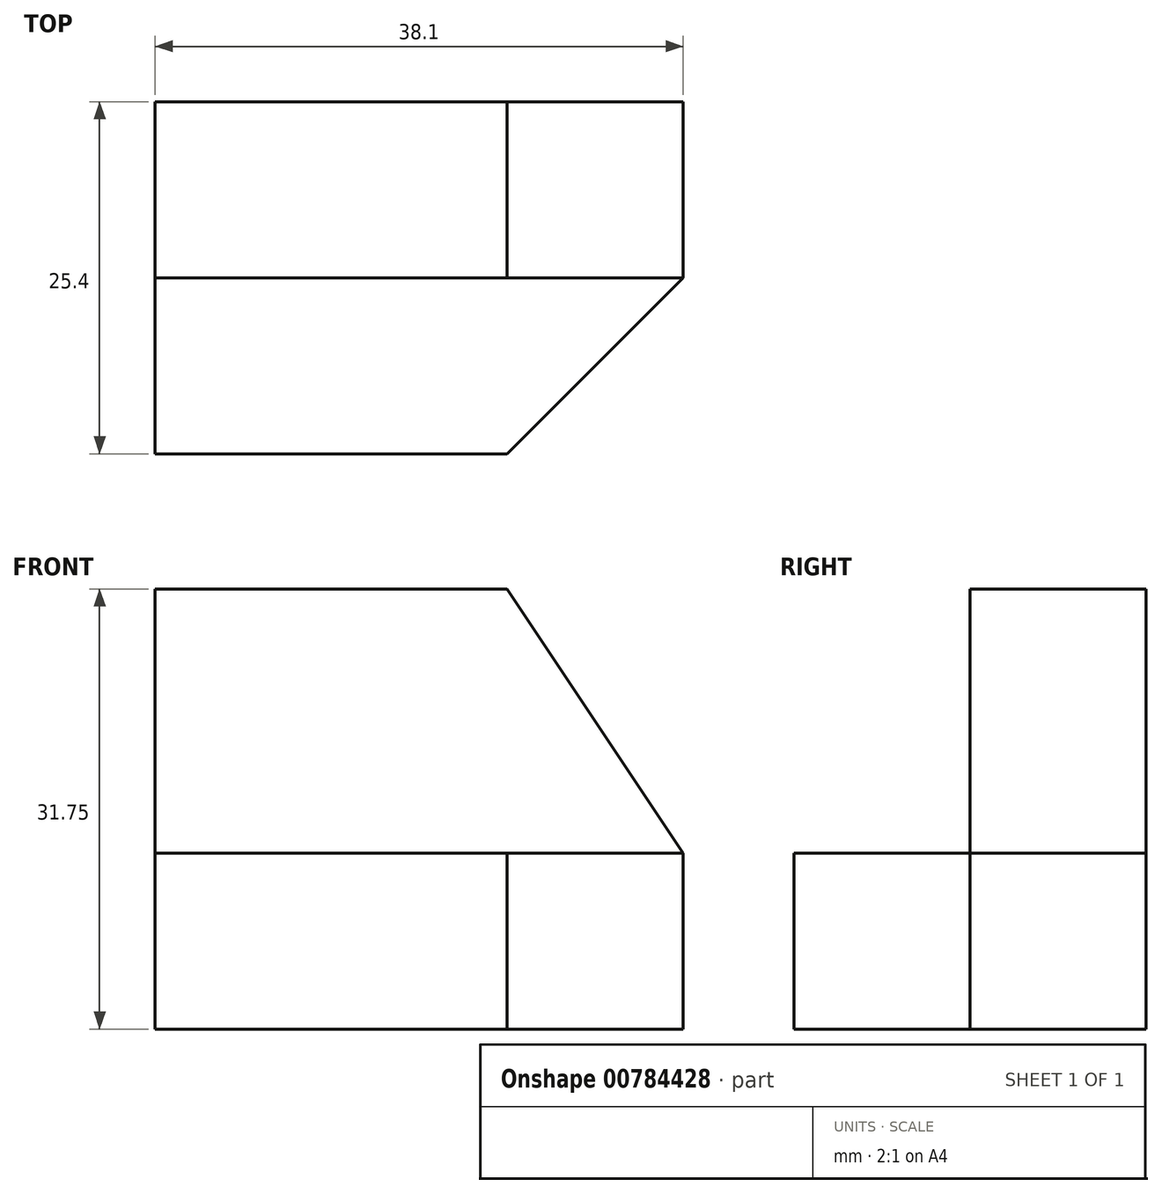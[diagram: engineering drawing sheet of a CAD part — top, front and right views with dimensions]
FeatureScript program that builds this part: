
annotation { "Feature Type Name" : "Feature", "Feature Type Description" : "" }
export const myFeature = defineFeature(function(context is Context, id is Id, definition is map)
    precondition{}
    {
        {
            var Q0;
            Q0=qCreatedBy(makeId("Front.planeOp"),FACE);
            var sketch = newSketch(context, id + "F0", { "sketchPlane" : qUnion([Q0])});
            skLineSegment(sketch, "E0", {"start": v(0, 0) * mm, "end": v(0, 31.75) * mm});
            skLineSegment(sketch, "E1", {"start": v(0, 31.75) * mm, "end": v(25.4, 31.75) * mm});
            skLineSegment(sketch, "E2", {"start": v(0, 0) * mm, "end": v(38.1, 0) * mm});
            skLineSegment(sketch, "E3", {"start": v(38.1, 0) * mm, "end": v(38.1, 12.7) * mm});
            skLineSegment(sketch, "E4", {"start": v(38.1, 12.7) * mm, "end": v(25.4, 31.75) * mm});
            skSolve(sketch);
        }
        {
            var Q0;
            Q0 = qSketchRegion(id + "F0", true);
            extrude(context, id + "F1", {"entities" : qUnion([Q0]), "depth" : 25.4 * mm, "offsetDistance" : 25.4 * mm});
        }
        {
            var Q0;
            Q0=makeQuery(id+"F1.opExtrude","SWEPT_FACE",FACE,{"disambiguationData":[OSD([sQuery(id+"F0.wireOp",EDGE,"E0")])]});
            var sketch = newSketch(context, id + "F2", { "sketchPlane" : qUnion([Q0])});
            skLineSegment(sketch, "E5", {"start": v(25.4, 31.75) * mm, "end": v(12.7, 31.75) * mm});
            skLineSegment(sketch, "E6", {"start": v(12.7, 31.75) * mm, "end": v(12.7, 12.7) * mm});
            skLineSegment(sketch, "E7", {"start": v(12.7, 12.7) * mm, "end": v(25.4, 12.7) * mm});
            skLineSegment(sketch, "E8", {"start": v(25.4, 12.7) * mm, "end": v(25.4, 31.75) * mm});
            skSolve(sketch);
        }
        {
            var Q0;
            Q0 = qSketchRegion(id + "F2", true);
            extrude(context, id + "F3", {"entities" : qUnion([Q0]), "operationType" : NewBodyOperationType.REMOVE, "oppositeDirection" : true, "depth" : 38.1 * mm, "offsetDistance" : 25.4 * mm});
        }
        {
            var Q0;
            Q0=makeQuery(id+"F3.boolean.opBoolean","COPY",FACE,{"derivedFrom":makeQuery(id+"F3.opExtrude","SWEPT_FACE",FACE,{"disambiguationData":[OSD([sQuery(id+"F2.wireOp",EDGE,"E7")])]})});
            var sketch = newSketch(context, id + "F4", { "sketchPlane" : qUnion([Q0])});
            skLineSegment(sketch, "E9", {"start": v(38.1, -25.4) * mm, "end": v(25.4, -25.4) * mm});
            skLineSegment(sketch, "E10", {"start": v(25.4, -25.4) * mm, "end": v(38.1, -12.7) * mm});
            skLineSegment(sketch, "E11", {"start": v(38.1, -12.7) * mm, "end": v(38.1, -25.4) * mm});
            skSolve(sketch);
        }
        {
            var Q0;
            Q0=makeQuery(id+"F4.imprint","IMPRINT",FACE,{"disambiguationData":[TD([[makeQuery(id+"F4.imprint","IMPRINT",EDGE,{"derivedFrom":sQuery(id+"F4.wireOp",EDGE,"E9")}),-1.0]])]});
            extrude(context, id + "F5", {"entities" : qUnion([Q0]), "operationType" : NewBodyOperationType.REMOVE, "oppositeDirection" : true, "depth" : 12.7 * mm, "offsetDistance" : 25.4 * mm});
        }
    });
